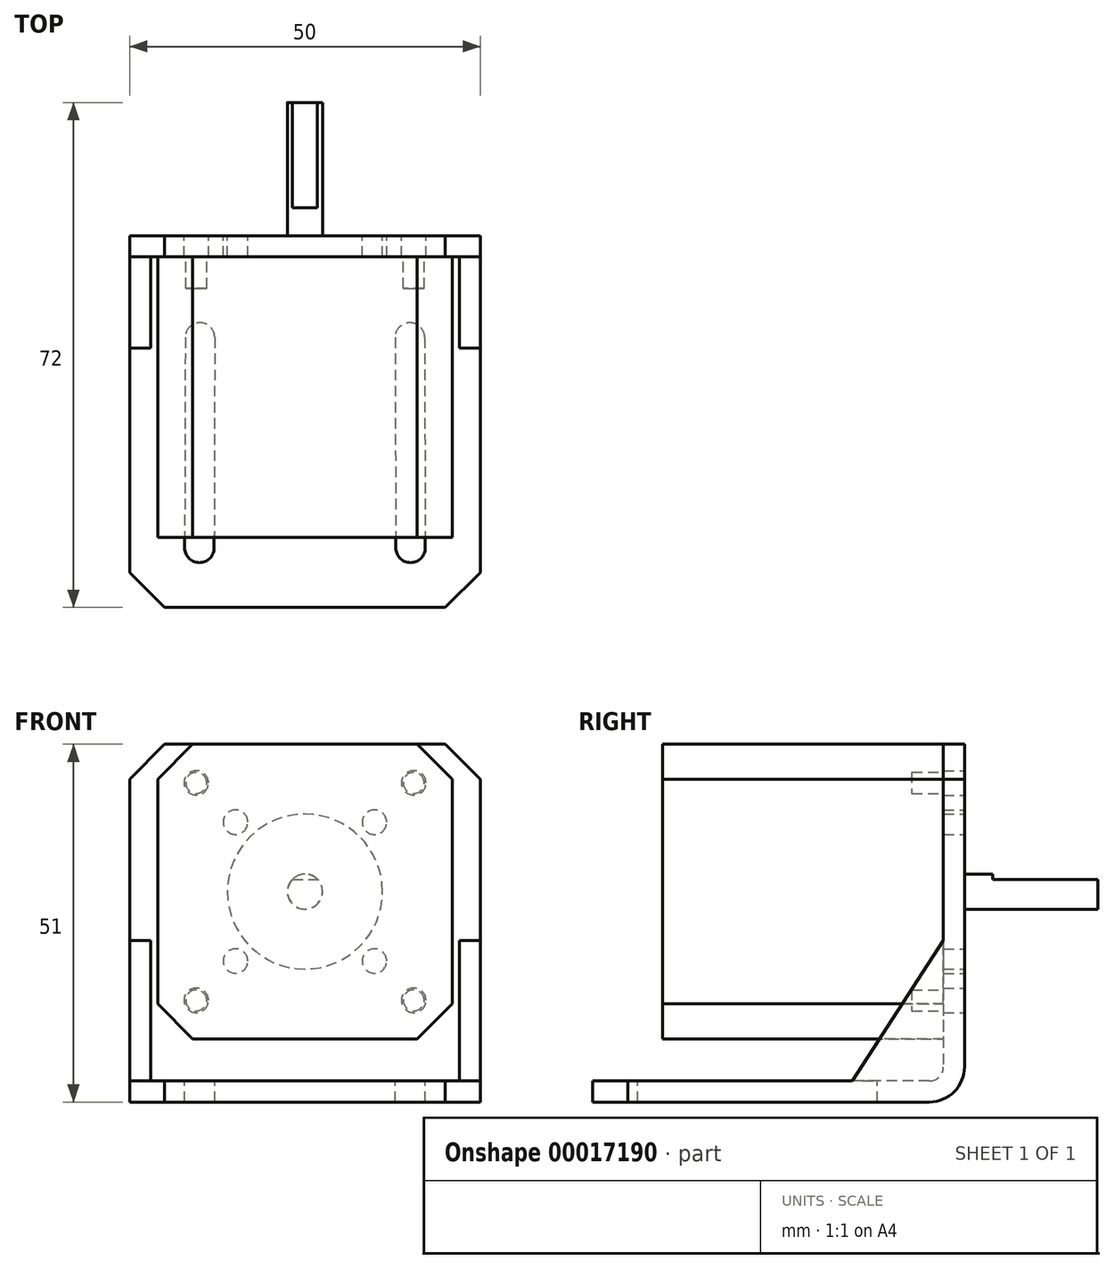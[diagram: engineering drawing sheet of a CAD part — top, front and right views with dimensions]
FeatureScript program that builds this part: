
annotation { "Feature Type Name" : "Feature", "Feature Type Description" : "" }
export const myFeature = defineFeature(function(context is Context, id is Id, definition is map)
    precondition{}
    {
        {
            var Q0;
            Q0=qCreatedBy(makeId("Front.planeOp"),FACE);
            var sketch = newSketch(context, id + "F0", { "sketchPlane" : qUnion([Q0])});
            skLineSegment(sketch, "E0.rect.bottom", {"start": v(21, -21) * mm, "end": v(-21, -21) * mm});
            skLineSegment(sketch, "E0.rect.top", {"start": v(21, 21) * mm, "end": v(-21, 21) * mm});
            skLineSegment(sketch, "E0.rect.left", {"start": v(21, -21) * mm, "end": v(21, 21) * mm});
            skLineSegment(sketch, "E0.rect.right", {"start": v(-21, -21) * mm, "end": v(-21, 21) * mm});
            skPoint(sketch, "E0.rect.middle", {"position": v(0, 0) * mm});
            skSolve(sketch);
        }
        {
            var Q0;
            Q0=qSketchRegion(id+"F0",true);
            extrude(context, id + "F1", {"entities" : qUnion([Q0]), "depth" : 40 * mm});
        }
        {
            var Q0;
            Q0=makeQuery(id+"F1.opExtrude","SWEPT_EDGE",EDGE,{"disambiguationData":[OSD([sQuery(id+"F0.wireOp",EDGE,"E0.rect.top"),sQuery(id+"F0.wireOp",EDGE,"E0.rect.left")])]});
            var Q1;
            Q1=makeQuery(id+"F1.opExtrude","SWEPT_EDGE",EDGE,{"disambiguationData":[OSD([sQuery(id+"F0.wireOp",EDGE,"E0.rect.bottom"),sQuery(id+"F0.wireOp",EDGE,"E0.rect.left")])]});
            var Q2;
            Q2=makeQuery(id+"F1.opExtrude","SWEPT_EDGE",EDGE,{"disambiguationData":[OSD([sQuery(id+"F0.wireOp",EDGE,"E0.rect.bottom"),sQuery(id+"F0.wireOp",EDGE,"E0.rect.right")])]});
            var Q3;
            Q3=makeQuery(id+"F1.opExtrude","SWEPT_EDGE",EDGE,{"disambiguationData":[OSD([sQuery(id+"F0.wireOp",EDGE,"E0.rect.top"),sQuery(id+"F0.wireOp",EDGE,"E0.rect.right")])]});
            chamfer(context, id + "F2", {"entities" : qUnion([Q0, Q1, Q2, Q3]), "width" : 5 * mm, "tangentPropagation" : true});
        }
        {
            var Q0;
            Q0=makeQuery(id+"F1.opExtrude","CAP_FACE",FACE,{"disambiguationData":[OSD([sQuery(id+"F0.wireOp",EDGE,"E0.rect.bottom"),sQuery(id+"F0.wireOp",EDGE,"E0.rect.top"),sQuery(id+"F0.wireOp",EDGE,"E0.rect.left"),sQuery(id+"F0.wireOp",EDGE,"E0.rect.right")])],"isStart":true});
            var sketch = newSketch(context, id + "F3", { "sketchPlane" : qUnion([Q0])});
            skCircle(sketch, "E1", {"center": v(0, 0) * mm, "radius": 11 * mm});
            skSolve(sketch);
        }
        {
            var Q0;
            Q0=qSketchRegion(id+"F3",true);
            extrude(context, id + "F4", {"entities" : qUnion([Q0]), "operationType" : NewBodyOperationType.ADD, "depth" : 2 * mm});
        }
        {
            var Q0;
            Q0=makeQuery(id+"F4.opExtrude","CAP_FACE",FACE,{"disambiguationData":[OSD([sQuery(id+"F3.wireOp",EDGE,"E1")])],"isStart":false});
            var sketch = newSketch(context, id + "F5", { "sketchPlane" : qUnion([Q0])});
            skCircle(sketch, "E2", {"center": v(0, 0) * mm, "radius": 2.5 * mm});
            skSolve(sketch);
        }
        {
            var Q0;
            Q0=qSketchRegion(id+"F5",true);
            extrude(context, id + "F6", {"entities" : qUnion([Q0]), "operationType" : NewBodyOperationType.ADD, "depth" : 20 * mm});
        }
        {
            var Q0;
            Q0=makeQuery(id+"F6.opExtrude","CAP_FACE",FACE,{"disambiguationData":[OSD([sQuery(id+"F5.wireOp",EDGE,"E2")])],"isStart":false});
            var sketch = newSketch(context, id + "F7", { "sketchPlane" : qUnion([Q0])});
            skLineSegment(sketch, "E3.bottom", {"start": v(3.08, 2.85) * mm, "end": v(-2.74, 2.85) * mm});
            skLineSegment(sketch, "E3.top", {"start": v(3.08, 1.75) * mm, "end": v(-2.74, 1.75) * mm});
            skLineSegment(sketch, "E3.left", {"start": v(3.08, 1.75) * mm, "end": v(3.08, 2.85) * mm});
            skLineSegment(sketch, "E3.right", {"start": v(-2.74, 1.75) * mm, "end": v(-2.74, 2.85) * mm});
            skSolve(sketch);
        }
        {
            var Q0;
            Q0=qSketchRegion(id+"F7",true);
            extrude(context, id + "F8", {"entities" : qUnion([Q0]), "operationType" : NewBodyOperationType.REMOVE, "oppositeDirection" : true, "depth" : 15 * mm});
        }
        {
            var Q0;
            Q0=makeQuery(id+"F1.opExtrude","CAP_FACE",FACE,{"disambiguationData":[OSD([sQuery(id+"F0.wireOp",EDGE,"E0.rect.bottom"),sQuery(id+"F0.wireOp",EDGE,"E0.rect.top"),sQuery(id+"F0.wireOp",EDGE,"E0.rect.left"),sQuery(id+"F0.wireOp",EDGE,"E0.rect.right")])],"isStart":true});
            var sketch = newSketch(context, id + "F9", { "sketchPlane" : qUnion([Q0])});
            skCircle(sketch, "E4", {"center": v(15.5, -15.5) * mm, "radius": 1.5 * mm});
            skCircle(sketch, "E5.0.1.0", {"center": v(15.5, 15.5) * mm, "radius": 1.5 * mm});
            skCircle(sketch, "E5.1.0.0", {"center": v(-15.5, -15.5) * mm, "radius": 1.5 * mm});
            skCircle(sketch, "E5.1.1.0", {"center": v(-15.5, 15.5) * mm, "radius": 1.5 * mm});
            skLineSegment(sketch, "E5.direction1", {"start": v(15.5, -15.5) * mm, "end": v(-15.5, -15.5) * mm, "construction": true});
            skLineSegment(sketch, "E5.direction2", {"start": v(15.5, -15.5) * mm, "end": v(15.5, 15.5) * mm, "construction": true});
            skSolve(sketch);
        }
        {
            var Q0;
            Q0=qSketchRegion(id+"F9",true);
            extrude(context, id + "F10", {"entities" : qUnion([Q0]), "operationType" : NewBodyOperationType.REMOVE, "oppositeDirection" : true, "depth" : 4.5 * mm});
        }
        {
            var Q0;
            Q0=qCreatedBy(makeId("Right.planeOp"),FACE);
            var sketch = newSketch(context, id + "F11", { "sketchPlane" : qUnion([Q0])});
            skLineSegment(sketch, "E6.bottom", {"start": v(0, 21) * mm, "end": v(3, 21) * mm});
            skLineSegment(sketch, "E6.left", {"start": v(0, 21) * mm, "end": v(0, -25) * mm});
            skLineSegment(sketch, "E7.bottom", {"start": v(-2, -27) * mm, "end": v(-50, -27) * mm});
            skLineSegment(sketch, "E7.top", {"start": v(-2, -30) * mm, "end": v(-50, -30) * mm});
            skLineSegment(sketch, "E7.right", {"start": v(-50, -27) * mm, "end": v(-50, -30) * mm});
            skLineSegment(sketch, "E8", {"start": v(3, 21) * mm, "end": v(3, -25) * mm});
            skPoint(sketch, "E9.visualSharp", {"position": v(0, -27) * mm});
            skArc(sketch, "E9.filletArc", {"start": v(-2, -27) * mm, "mid": v(-0.59, -26.41) * mm, "end": v(0, -25) * mm});
            skPoint(sketch, "E10.visualSharp", {"position": v(3, -30) * mm});
            skArc(sketch, "E10.filletArc", {"start": v(-2, -30) * mm, "mid": v(1.54, -28.54) * mm, "end": v(3, -25) * mm});
            skSolve(sketch);
        }
        {
            var Q0;
            Q0=qSketchRegion(id+"F11",true);
            extrude(context, id + "F12", {"entities" : qUnion([Q0]), "endBound" : BoundingType.SYMMETRIC, "depth" : 50 * mm});
        }
        {
            var Q0;
            Q0=makeQuery(id+"F12.opExtrude","SWEPT_FACE",FACE,{"disambiguationData":[OSD([sQuery(id+"F11.wireOp",EDGE,"E8")])]});
            var sketch = newSketch(context, id + "F13", { "sketchPlane" : qUnion([Q0])});
            skCircle(sketch, "E11", {"center": v(0, 0) * mm, "radius": 11.05 * mm});
            skCircle(sketch, "E12", {"center": v(-15.5, 15.5) * mm, "radius": 1.75 * mm});
            skCircle(sketch, "E13.0.1.0", {"center": v(-15.5, -15.5) * mm, "radius": 1.75 * mm});
            skCircle(sketch, "E13.1.0.0", {"center": v(15.5, 15.5) * mm, "radius": 1.75 * mm});
            skCircle(sketch, "E13.1.1.0", {"center": v(15.5, -15.5) * mm, "radius": 1.75 * mm});
            skLineSegment(sketch, "E13.direction1", {"start": v(-15.5, 15.5) * mm, "end": v(15.5, 15.5) * mm, "construction": true});
            skLineSegment(sketch, "E13.direction2", {"start": v(-15.5, 15.5) * mm, "end": v(-15.5, -15.5) * mm, "construction": true});
            skCircle(sketch, "E14", {"center": v(0, 0) * mm, "radius": 14 * mm, "construction": true});
            skCircle(sketch, "E15", {"center": v(9.9, 9.9) * mm, "radius": 1.75 * mm});
            skCircle(sketch, "E16.1.0", {"center": v(-9.9, 9.9) * mm, "radius": 1.75 * mm});
            skCircle(sketch, "E16.2.0", {"center": v(-9.9, -9.9) * mm, "radius": 1.75 * mm});
            skCircle(sketch, "E16.3.0", {"center": v(9.9, -9.9) * mm, "radius": 1.75 * mm});
            skSolve(sketch);
        }
        {
            var Q0;
            Q0=qSketchRegion(id+"F13",true);
            var Q1;
            Q1=makeQuery(id+"F12.opExtrude","SWEPT_FACE",FACE,{"disambiguationData":[OSD([sQuery(id+"F11.wireOp",EDGE,"E6.left")])]});
            extrude(context, id + "F14", {"entities" : qUnion([Q0]), "operationType" : NewBodyOperationType.REMOVE, "endBound" : BoundingType.UP_TO_SURFACE, "oppositeDirection" : true, "endBoundEntityFace" : qUnion([Q1]), "depth" : 25 * mm});
        }
        {
            var Q0;
            Q0=makeQuery(id+"F12.opExtrude","CAP_EDGE",EDGE,{"disambiguationData":[OSD([sQuery(id+"F11.wireOp",EDGE,"E6.bottom")])],"isStart":true});
            var Q1;
            Q1=makeQuery(id+"F12.opExtrude","CAP_EDGE",EDGE,{"disambiguationData":[OSD([sQuery(id+"F11.wireOp",EDGE,"E6.bottom")])],"isStart":false});
            var Q2;
            Q2=makeQuery(id+"F12.opExtrude","CAP_EDGE",EDGE,{"disambiguationData":[OSD([sQuery(id+"F11.wireOp",EDGE,"E7.right")])],"isStart":false});
            var Q3;
            Q3=makeQuery(id+"F12.opExtrude","CAP_EDGE",EDGE,{"disambiguationData":[OSD([sQuery(id+"F11.wireOp",EDGE,"E7.right")])],"isStart":true});
            chamfer(context, id + "F15", {"entities" : qUnion([Q0, Q1, Q2, Q3]), "width" : 5 * mm, "tangentPropagation" : true});
        }
        {
            var Q0;
            Q0=makeQuery(id+"F12.opExtrude","SWEPT_FACE",FACE,{"disambiguationData":[OSD([sQuery(id+"F11.wireOp",EDGE,"E7.bottom")])]});
            var sketch = newSketch(context, id + "F16", { "sketchPlane" : qUnion([Q0])});
            skLineSegment(sketch, "E17.rect.left", {"start": v(-12.86, -11.5) * mm, "end": v(-12.94, -41.5) * mm});
            skLineSegment(sketch, "E17.rect.right", {"start": v(-17.06, -11.5) * mm, "end": v(-17.14, -41.5) * mm});
            skPoint(sketch, "E17.rect.middle", {"position": v(-15, -26.5) * mm});
            skArc(sketch, "E18", {"start": v(-12.86, -11.5) * mm, "mid": v(-14.95, -9.4) * mm, "end": v(-17.06, -11.5) * mm});
            skArc(sketch, "E19", {"start": v(-17.14, -41.5) * mm, "mid": v(-15.05, -43.6) * mm, "end": v(-12.94, -41.5) * mm});
            skLineSegment(sketch, "E20", {"start": v(0, 7.35) * mm, "end": v(0, 3.66) * mm, "construction": true});
            skArc(sketch, "E21.MirrorCS", {"start": v(12.86, -11.5) * mm, "mid": v(14.95, -9.4) * mm, "end": v(17.06, -11.5) * mm});
            skArc(sketch, "E22.MirrorCS", {"start": v(17.14, -41.5) * mm, "mid": v(15.05, -43.6) * mm, "end": v(12.94, -41.5) * mm});
            skPoint(sketch, "E23.MirrorP", {"position": v(15, -26.5) * mm});
            skLineSegment(sketch, "E24.MirrorCS", {"start": v(12.86, -11.5) * mm, "end": v(12.94, -41.5) * mm});
            skLineSegment(sketch, "E25.MirrorCS", {"start": v(17.06, -11.5) * mm, "end": v(17.14, -41.5) * mm});
            skSolve(sketch);
        }
        {
            var Q0;
            Q0=qSketchRegion(id+"F16",true);
            var Q1;
            Q1=makeQuery(id+"F12.opExtrude","SWEPT_FACE",FACE,{"disambiguationData":[OSD([sQuery(id+"F11.wireOp",EDGE,"E7.top")])]});
            extrude(context, id + "F17", {"entities" : qUnion([Q0]), "operationType" : NewBodyOperationType.REMOVE, "endBound" : BoundingType.UP_TO_SURFACE, "oppositeDirection" : true, "endBoundEntityFace" : qUnion([Q1]), "depth" : 25 * mm});
        }
        {
            var Q0;
            Q0=makeQuery(id+"F12.opExtrude","CAP_FACE",FACE,{"disambiguationData":[OSD([sQuery(id+"F11.wireOp",EDGE,"E6.bottom"),sQuery(id+"F11.wireOp",EDGE,"E6.left"),sQuery(id+"F11.wireOp",EDGE,"E7.bottom"),sQuery(id+"F11.wireOp",EDGE,"E7.top"),sQuery(id+"F11.wireOp",EDGE,"E7.right"),sQuery(id+"F11.wireOp",EDGE,"E8"),sQuery(id+"F11.wireOp",EDGE,"E9.filletArc"),sQuery(id+"F11.wireOp",EDGE,"E10.filletArc")])],"isStart":true});
            var sketch = newSketch(context, id + "F18", { "sketchPlane" : qUnion([Q0])});
            skLineSegment(sketch, "E26", {"start": v(0, -7) * mm, "end": v(13, -27) * mm});
            skLineSegment(sketch, "E27", {"start": v(13, -27) * mm, "end": v(0, -27) * mm});
            skLineSegment(sketch, "E28", {"start": v(0, -27) * mm, "end": v(0, -7) * mm});
            skSolve(sketch);
        }
        {
            var Q0;
            Q0=qSketchRegion(id+"F18",true);
            extrude(context, id + "F19", {"entities" : qUnion([Q0]), "oppositeDirection" : true, "depth" : 3 * mm});
        }
        {
            var Q0;
            Q0=makeQuery(id+"F19.opExtrude","SWEPT_BODY",BODY,{"disambiguationData":[OSD([sQuery(id+"F18.wireOp",EDGE,"E26"),sQuery(id+"F18.wireOp",EDGE,"E27"),sQuery(id+"F18.wireOp",EDGE,"E28")])]});
            var Q1;
            Q1=qCreatedBy(makeId("Right.planeOp"),FACE);
            mirror(context, id + "F20", {"operationType" : NewBodyOperationType.ADD, "entities" : qUnion([Q0]), "mirrorPlane" : qUnion([Q1])});
        }
    });
